# Revit family: Sink-Undermount-Lavatory-KOHLER-VERTICYL-K-2882T_1
name_source: partatom
category: Plumbing Fixtures
units: mm (PartAtom-declared; Revit-internal decimal feet)

## family parameters
Cut with Voids When Loaded = No
Host = Face
OmniClass Number = 23.31.13.00
OmniClass Title = Sinks
Part Type = Normal
Room Calculation Point = No
Round Connector Dimension = Use Diameter
Shared = No

## types (3) — shared parameters
ADA Compliant = No
Assembly Code = D2010400
CW Connection = No
Cold Water Inlet = Cold Water Inlet
Date Modified = 11/21/2023
Default Elevation = 36"
Description = Rectangular undermount basin
Drain Included = No
Flow Rate = 0 GPM
HW Connection = No
Height = 6 3/4"
Hot Water Inlet = Hot Water Inlet
Length = 19 13/16"
Manufacturer = Kohler Co.
Master Format 2014 = 22 41 16
Master Format 2014 Name = Residential Lavatories and Sinks
Material = Vitreous China
Pressure = 0.00 psi
Product Documentation Link = https://files.kohler.com.cn
Product Name = Verticyl
URL = http://www.kohler.com.cn
Vent Connection = No
Waste Connection = Yes
Waste Water Outlet = Waste Water Outlet
WaterSense Certified = No
Width = 15 5/8"

## per-type parameters (varying)
| type | Finish | Model | Product Page URL | Type |
| 0-White | Kohler-Vitreous_China-0-White | K-2882T-0 | https://www.kohler.com.cn | 1 |
| 17-Teal | KOHLER-Vitreous_China-17-Teal | K-2882T-17 |  | 2 |
| 42-Aspen Green | KOHLER-Vitreous_China-42-Aspen_Green | K-2882T-42 |  | 3 |

## geometry (parser evidence)
native form markers: Sweep x6
no freeform markers — native parametric forms only
